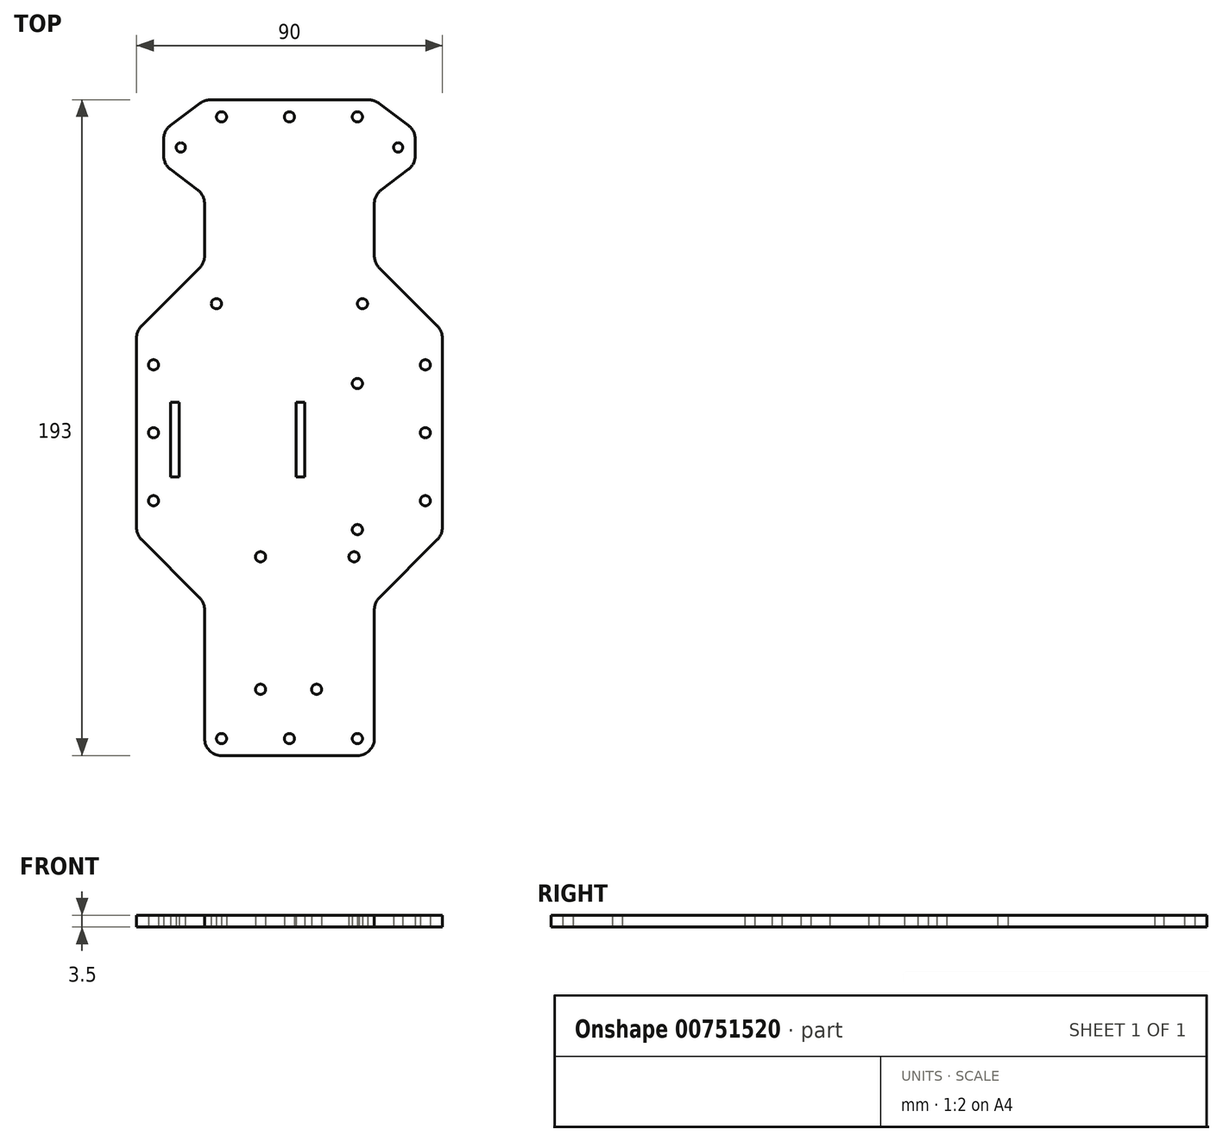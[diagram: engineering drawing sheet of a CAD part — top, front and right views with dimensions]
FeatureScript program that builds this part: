
annotation { "Feature Type Name" : "Feature", "Feature Type Description" : "" }
export const myFeature = defineFeature(function(context is Context, id is Id, definition is map)
    precondition{}
    {
        {
            var Q0;
            Q0=qCreatedBy(makeId("Top.planeOp"),FACE);
            var sketch = newSketch(context, id + "F0", { "sketchPlane" : qUnion([Q0])});
            skPoint(sketch, "E0.middle", {"position": v(0, 0) * mm});
            skLineSegment(sketch, "E1.left", {"start": v(-45, 32) * mm, "end": v(-45, -28) * mm});
            skLineSegment(sketch, "E1.right", {"start": v(45, 32) * mm, "end": v(45, -28) * mm});
            skLineSegment(sketch, "E2.bottom", {"start": v(-25, 100) * mm, "end": v(25, 100) * mm});
            skLineSegment(sketch, "E2.top", {"start": v(-20, -93) * mm, "end": v(20, -93) * mm});
            skLineSegment(sketch, "E2.right", {"start": v(25, 72) * mm, "end": v(25, 52) * mm});
            skLineSegment(sketch, "E3.trimOffspring", {"start": v(-25, -48) * mm, "end": v(-25, -88) * mm});
            skLineSegment(sketch, "E4.trimOffspring", {"start": v(25, -48) * mm, "end": v(25, -88) * mm});
            skLineSegment(sketch, "E5", {"start": v(-25, 100) * mm, "end": v(-37, 91) * mm});
            skLineSegment(sketch, "E6", {"start": v(-37, 91) * mm, "end": v(-37, 81) * mm});
            skLineSegment(sketch, "E7", {"start": v(-37, 81) * mm, "end": v(-25, 72) * mm});
            skLineSegment(sketch, "E8.MirrorCS", {"start": v(37, 81) * mm, "end": v(25, 72) * mm});
            skLineSegment(sketch, "E9.MirrorCS", {"start": v(37, 91) * mm, "end": v(37, 81) * mm});
            skLineSegment(sketch, "E10.MirrorCS", {"start": v(25, 100) * mm, "end": v(37, 91) * mm});
            skCircle(sketch, "E11", {"center": v(-32, 86) * mm, "radius": 1.38 * mm});
            skLineSegment(sketch, "E12", {"start": v(-32, 86) * mm, "end": v(-32, 94.75) * mm, "construction": true});
            skLineSegment(sketch, "E13", {"start": v(-32, 86) * mm, "end": v(-32, 77.25) * mm, "construction": true});
            skLineSegment(sketch, "E14", {"start": v(-45, 32) * mm, "end": v(-25, 52) * mm});
            skLineSegment(sketch, "E15", {"start": v(45, 32) * mm, "end": v(25, 52) * mm});
            skLineSegment(sketch, "E16", {"start": v(-45, -28) * mm, "end": v(-25, -48) * mm});
            skLineSegment(sketch, "E17", {"start": v(45, -28) * mm, "end": v(25, -48) * mm});
            skCircle(sketch, "E18", {"center": v(0, 95) * mm, "radius": 1.5 * mm});
            skCircle(sketch, "E19", {"center": v(-20, 95) * mm, "radius": 1.5 * mm});
            skCircle(sketch, "E20", {"center": v(21.5, 40) * mm, "radius": 1.5 * mm});
            skCircle(sketch, "E21", {"center": v(-21.5, 40) * mm, "radius": 1.5 * mm});
            skPoint(sketch, "E22.visualSharp", {"position": v(25, -93) * mm});
            skArc(sketch, "E22.filletArc", {"start": v(20, -93) * mm, "mid": v(23.54, -91.54) * mm, "end": v(25, -88) * mm});
            skPoint(sketch, "E23.visualSharp", {"position": v(-25, -93) * mm});
            skArc(sketch, "E23.filletArc", {"start": v(-25, -88) * mm, "mid": v(-23.54, -91.54) * mm, "end": v(-20, -93) * mm});
            skLineSegment(sketch, "E24.trimOffspring", {"start": v(-25, 72) * mm, "end": v(-25, 52) * mm});
            skCircle(sketch, "E25", {"center": v(32, 86) * mm, "radius": 1.38 * mm});
            skLineSegment(sketch, "E26", {"start": v(32, 86) * mm, "end": v(32, 94.75) * mm, "construction": true});
            skLineSegment(sketch, "E27", {"start": v(32, 86) * mm, "end": v(32, 77.25) * mm, "construction": true});
            skLineSegment(sketch, "E28", {"start": v(-32, 86) * mm, "end": v(-37, 86) * mm, "construction": true});
            skLineSegment(sketch, "E29", {"start": v(32, 86) * mm, "end": v(37, 86) * mm, "construction": true});
            skCircle(sketch, "E30", {"center": v(20, 95) * mm, "radius": 1.5 * mm});
            skLineSegment(sketch, "E31", {"start": v(0, 95) * mm, "end": v(-20, 95) * mm, "construction": true});
            skLineSegment(sketch, "E32", {"start": v(0, 95) * mm, "end": v(20, 95) * mm, "construction": true});
            skCircle(sketch, "E33", {"center": v(0, -88) * mm, "radius": 1.5 * mm});
            skCircle(sketch, "E34", {"center": v(-20, -88) * mm, "radius": 1.5 * mm});
            skCircle(sketch, "E35", {"center": v(20, -88) * mm, "radius": 1.5 * mm});
            skPoint(sketch, "E36", {"position": v(0, -93) * mm});
            skLineSegment(sketch, "E37", {"start": v(0, -88) * mm, "end": v(-20, -88) * mm, "construction": true});
            skLineSegment(sketch, "E38", {"start": v(0, -88) * mm, "end": v(20, -88) * mm, "construction": true});
            skLineSegment(sketch, "E39", {"start": v(-25, -82) * mm, "end": v(25, -82) * mm, "construction": true});
            skCircle(sketch, "E40", {"center": v(-8.5, -34.5) * mm, "radius": 1.5 * mm});
            skCircle(sketch, "E41.MirrorC", {"center": v(19, -34.5) * mm, "radius": 1.5 * mm});
            skCircle(sketch, "E42", {"center": v(-8.5, -73.5) * mm, "radius": 1.5 * mm});
            skLineSegment(sketch, "E43", {"start": v(0, -30.5) * mm, "end": v(24.04, -30.5) * mm, "construction": true});
            skCircle(sketch, "E44", {"center": v(8, -73.5) * mm, "radius": 1.5 * mm});
            skCircle(sketch, "E45", {"center": v(-40, 22) * mm, "radius": 1.5 * mm});
            skCircle(sketch, "E46", {"center": v(-40, 2) * mm, "radius": 1.5 * mm});
            skCircle(sketch, "E47", {"center": v(-40, -18) * mm, "radius": 1.5 * mm});
            skCircle(sketch, "E48", {"center": v(40, 22) * mm, "radius": 1.5 * mm});
            skCircle(sketch, "E49", {"center": v(40, 2) * mm, "radius": 1.5 * mm});
            skCircle(sketch, "E50", {"center": v(40, -18) * mm, "radius": 1.5 * mm});
            skCircle(sketch, "E51", {"center": v(20, 16.5) * mm, "radius": 1.5 * mm});
            skCircle(sketch, "E52", {"center": v(20, -26.5) * mm, "radius": 1.5 * mm});
            skLineSegment(sketch, "E53.bottom", {"start": v(-35, 11) * mm, "end": v(-32.5, 11) * mm});
            skLineSegment(sketch, "E53.top", {"start": v(-35, -11) * mm, "end": v(-32.5, -11) * mm});
            skLineSegment(sketch, "E53.left", {"start": v(-35, 11) * mm, "end": v(-35, -11) * mm});
            skLineSegment(sketch, "E53.right", {"start": v(-32.5, 11) * mm, "end": v(-32.5, -11) * mm});
            skLineSegment(sketch, "E54.bottom", {"start": v(-30, 27) * mm, "end": v(0, 27) * mm, "construction": true});
            skLineSegment(sketch, "E54.top", {"start": v(-30, -27) * mm, "end": v(0, -27) * mm, "construction": true});
            skLineSegment(sketch, "E54.left", {"start": v(-30, 27) * mm, "end": v(-30, -27) * mm, "construction": true});
            skLineSegment(sketch, "E54.right", {"start": v(0, 27) * mm, "end": v(0, -27) * mm, "construction": true});
            skLineSegment(sketch, "E55.bottom", {"start": v(2, 11) * mm, "end": v(4.5, 11) * mm});
            skLineSegment(sketch, "E55.top", {"start": v(2, -11) * mm, "end": v(4.5, -11) * mm});
            skLineSegment(sketch, "E55.left", {"start": v(2, 11) * mm, "end": v(2, -11) * mm});
            skLineSegment(sketch, "E55.right", {"start": v(4.5, 11) * mm, "end": v(4.5, -11) * mm});
            skLineSegment(sketch, "E56", {"start": v(-21.5, 40) * mm, "end": v(-25, 40) * mm, "construction": true});
            skLineSegment(sketch, "E57", {"start": v(21.5, 40) * mm, "end": v(25, 40) * mm, "construction": true});
            skPoint(sketch, "E58", {"position": v(-45, 2) * mm});
            skSolve(sketch);
        }
        {
            var Q0;
            {var subQ5=sQuery(id+"F0.wireOp",EDGE,"E1.bottom");Q0=makeQuery(id+"F0.imprint","IMPRINT",FACE,{"disambiguationData":[TD([[makeQuery(id+"F0.imprint","IMPRINT",EDGE,{"derivedFrom":subQ5}),-1.0]])]});}
            var Q1;
            {var subQ0=sQuery(id+"F0.wireOp",EDGE,"E1.bottom");Q1=makeQuery(id+"F0.imprint","IMPRINT",FACE,{"disambiguationData":[TD([[makeQuery(id+"F0.imprint","IMPRINT",EDGE,{"derivedFrom":subQ0}),1.0]])]});}
            var Q2;
            {var subQ2=sQuery(id+"F0.wireOp",EDGE,"mY936AxS-bCtM-u6mH-qkgE-3i1a7G4UpAxP");Q2=makeQuery(id+"F0.imprint","IMPRINT",FACE,{"disambiguationData":[TD([[makeQuery(id+"F0.imprint","IMPRINT",EDGE,{"derivedFrom":subQ2}),1.0]])]});}
            var Q3;
            {var subQ0=sQuery(id+"F0.wireOp",EDGE,"tlpUXb4p-dup2-cb7J-fJeQ-cunatJqCv4r3");Q3=makeQuery(id+"F0.imprint","IMPRINT",FACE,{"disambiguationData":[TD([[makeQuery(id+"F0.imprint","IMPRINT",EDGE,{"derivedFrom":subQ0}),-1.0]])]});}
            var Q4;
            {var subQ0=sQuery(id+"F0.wireOp",EDGE,"E1.top");Q4=makeQuery(id+"F0.imprint","IMPRINT",FACE,{"disambiguationData":[TD([[makeQuery(id+"F0.imprint","IMPRINT",EDGE,{"derivedFrom":subQ0}),-1.0]])]});}
            var Q5;
            {var subQ0=sQuery(id+"F0.wireOp",EDGE,"E5");Q5=makeQuery(id+"F0.imprint","IMPRINT",FACE,{"disambiguationData":[TD([[makeQuery(id+"F0.imprint","IMPRINT",EDGE,{"derivedFrom":subQ0}),1.0]])]});}
            var Q6;
            {var subQ0=sQuery(id+"F0.wireOp",EDGE,"pqNEKcwJ-h33T-HL2r-peva-7RRUNKeUBN5d");Q6=makeQuery(id+"F0.imprint","IMPRINT",FACE,{"disambiguationData":[TD([[makeQuery(id+"F0.imprint","IMPRINT",EDGE,{"derivedFrom":subQ0}),-1.0]])]});}
            var Q7;
            {var subQ0=sQuery(id+"F0.wireOp",EDGE,"a00ee1d5-904a-4f26-b629-e24fb3101e3a.trimOffspring");Q7=makeQuery(id+"F0.imprint","IMPRINT",FACE,{"disambiguationData":[TD([[makeQuery(id+"F0.imprint","IMPRINT",EDGE,{"derivedFrom":subQ0}),1.0]])]});}
            var Q8;
            {var subQ0=sQuery(id+"F0.wireOp",EDGE,"a8a4ccb4-9108-42de-b2b3-bf1162c27bd3.trimOffspring");Q8=makeQuery(id+"F0.imprint","IMPRINT",FACE,{"disambiguationData":[TD([[makeQuery(id+"F0.imprint","IMPRINT",EDGE,{"derivedFrom":subQ0}),-1.0]])]});}
            var Q9;
            {var subQ2=sQuery(id+"F0.wireOp",EDGE,"22062ab9-91ba-4eca-898b-d4dce9db847a0.MirrorCS");Q9=makeQuery(id+"F0.imprint","IMPRINT",FACE,{"disambiguationData":[TD([[makeQuery(id+"F0.imprint","IMPRINT",EDGE,{"derivedFrom":subQ2}),1.0]])]});}
            var Q10;
            {var subQ0=sQuery(id+"F0.wireOp",EDGE,"326a62c6-d771-4757-9c2b-3534473035e10.MirrorCS");Q10=makeQuery(id+"F0.imprint","IMPRINT",FACE,{"disambiguationData":[TD([[makeQuery(id+"F0.imprint","IMPRINT",EDGE,{"derivedFrom":subQ0}),-1.0]])]});}
            var Q11;
            {var subQ2=sQuery(id+"F0.wireOp",EDGE,"E8.MirrorCS");Q11=makeQuery(id+"F0.imprint","IMPRINT",FACE,{"disambiguationData":[TD([[makeQuery(id+"F0.imprint","IMPRINT",EDGE,{"derivedFrom":subQ2}),-1.0]])]});}
            extrude(context, id + "F1", {"entities" : qUnion([Q0, Q1, Q2, Q3, Q4, Q5, Q6, Q7, Q8, Q9, Q10, Q11]), "depth" : 3.5 * mm, "offsetDistance" : 25 * mm});
        }
        {
            var Q0;
            Q0=makeQuery(id+"F1.opExtrude","SWEPT_EDGE",EDGE,{"disambiguationData":[OSD([sQuery(id+"F0.wireOp",EDGE,"E1.left"),sQuery(id+"F0.wireOp",EDGE,"E16")])]});
            var Q1;
            Q1=makeQuery(id+"F1.opExtrude","SWEPT_EDGE",EDGE,{"disambiguationData":[OSD([sQuery(id+"F0.wireOp",EDGE,"E3.trimOffspring"),sQuery(id+"F0.wireOp",EDGE,"E16")])]});
            var Q2;
            Q2=makeQuery(id+"F1.opExtrude","SWEPT_EDGE",EDGE,{"disambiguationData":[OSD([sQuery(id+"F0.wireOp",EDGE,"E4.trimOffspring"),sQuery(id+"F0.wireOp",EDGE,"E17")])]});
            var Q3;
            Q3=makeQuery(id+"F1.opExtrude","SWEPT_EDGE",EDGE,{"disambiguationData":[OSD([sQuery(id+"F0.wireOp",EDGE,"E1.right"),sQuery(id+"F0.wireOp",EDGE,"E17")])]});
            var Q4;
            Q4=makeQuery(id+"F1.opExtrude","SWEPT_EDGE",EDGE,{"disambiguationData":[OSD([sQuery(id+"F0.wireOp",EDGE,"E1.right"),sQuery(id+"F0.wireOp",EDGE,"E15")])]});
            var Q5;
            Q5=makeQuery(id+"F1.opExtrude","SWEPT_EDGE",EDGE,{"disambiguationData":[OSD([sQuery(id+"F0.wireOp",EDGE,"E2.right"),sQuery(id+"F0.wireOp",EDGE,"E15")])]});
            var Q6;
            Q6=makeQuery(id+"F1.opExtrude","SWEPT_EDGE",EDGE,{"disambiguationData":[OSD([sQuery(id+"F0.wireOp",EDGE,"E2.right"),sQuery(id+"F0.wireOp",EDGE,"E8.MirrorCS")])]});
            var Q7;
            Q7=makeQuery(id+"F1.opExtrude","SWEPT_EDGE",EDGE,{"disambiguationData":[OSD([sQuery(id+"F0.wireOp",EDGE,"E14"),sQuery(id+"F0.wireOp",EDGE,"E24.trimOffspring")])]});
            var Q8;
            Q8=makeQuery(id+"F1.opExtrude","SWEPT_EDGE",EDGE,{"disambiguationData":[OSD([sQuery(id+"F0.wireOp",EDGE,"E1.left"),sQuery(id+"F0.wireOp",EDGE,"E14")])]});
            var Q9;
            Q9=makeQuery(id+"F1.opExtrude","SWEPT_EDGE",EDGE,{"disambiguationData":[OSD([sQuery(id+"F0.wireOp",EDGE,"E7"),sQuery(id+"F0.wireOp",EDGE,"E24.trimOffspring")])]});
            var Q10;
            Q10=makeQuery(id+"F1.opExtrude","SWEPT_EDGE",EDGE,{"disambiguationData":[OSD([sQuery(id+"F0.wireOp",EDGE,"E6"),sQuery(id+"F0.wireOp",EDGE,"E7")])]});
            var Q11;
            Q11=makeQuery(id+"F1.opExtrude","SWEPT_EDGE",EDGE,{"disambiguationData":[OSD([sQuery(id+"F0.wireOp",EDGE,"E5"),sQuery(id+"F0.wireOp",EDGE,"E6")])]});
            var Q12;
            Q12=makeQuery(id+"F1.opExtrude","SWEPT_EDGE",EDGE,{"disambiguationData":[OSD([sQuery(id+"F0.wireOp",EDGE,"E2.bottom"),sQuery(id+"F0.wireOp",EDGE,"E5")])]});
            var Q13;
            Q13=makeQuery(id+"F1.opExtrude","SWEPT_EDGE",EDGE,{"disambiguationData":[OSD([sQuery(id+"F0.wireOp",EDGE,"E2.bottom"),sQuery(id+"F0.wireOp",EDGE,"E10.MirrorCS")])]});
            var Q14;
            Q14=makeQuery(id+"F1.opExtrude","SWEPT_EDGE",EDGE,{"disambiguationData":[OSD([sQuery(id+"F0.wireOp",EDGE,"E9.MirrorCS"),sQuery(id+"F0.wireOp",EDGE,"E10.MirrorCS")])]});
            var Q15;
            Q15=makeQuery(id+"F1.opExtrude","SWEPT_EDGE",EDGE,{"disambiguationData":[OSD([sQuery(id+"F0.wireOp",EDGE,"E8.MirrorCS"),sQuery(id+"F0.wireOp",EDGE,"E9.MirrorCS")])]});
            fillet(context, id + "F2", {"entities" : qUnion([Q0, Q1, Q2, Q3, Q4, Q5, Q6, Q7, Q8, Q9, Q10, Q11, Q12, Q13, Q14, Q15]), "radius" : 5 * mm, "tangentPropagation" : true, "allowEdgeOverflow" : false});
        }
    });
